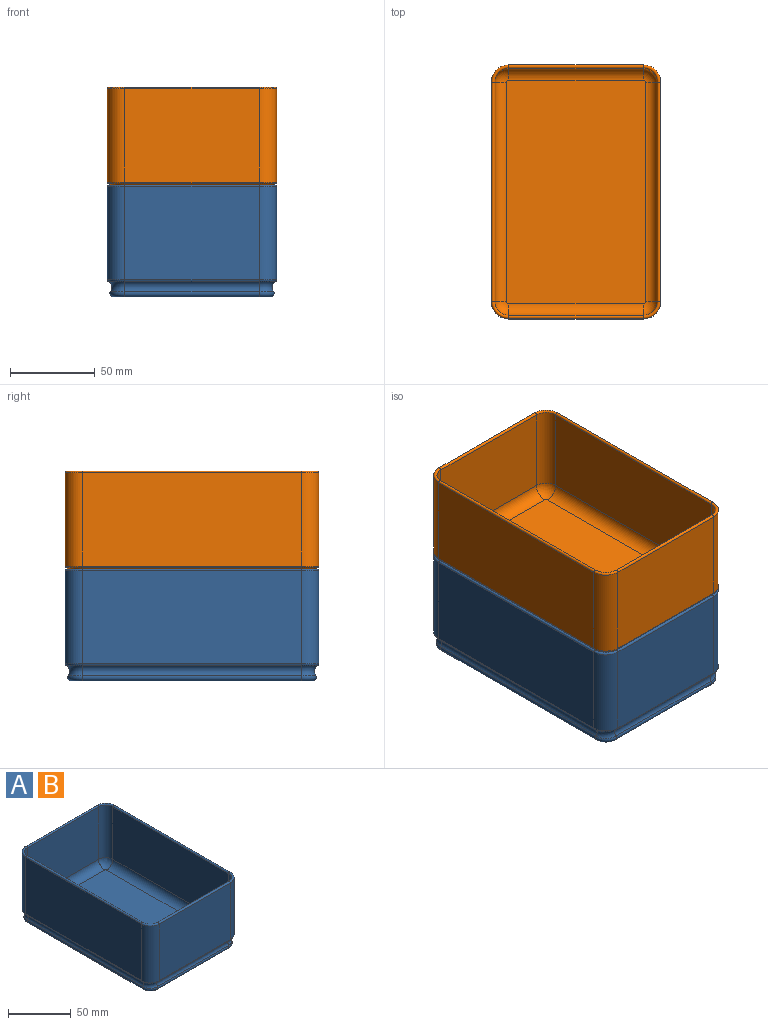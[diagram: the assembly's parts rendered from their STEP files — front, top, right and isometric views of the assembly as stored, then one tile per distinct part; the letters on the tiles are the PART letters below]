
ASSEMBLY  parts=2 mates=1
PART A: 66 faces, bbox 104.5x154.5x66 mm
  f0: torus R=0.68mm, axis (0,0,1), area 27mm2, adj f1,f8,f56,f65
  f1: torus R=6.6mm, axis (0,0,1), area 79.7mm2, adj f0,f2,f9,f57
  f2: torus R=11.42mm, axis (0,0,1), area 86.6mm2, adj f1,f3,f10,f58
  f3: torus R=9.1mm, axis (0,0,1), area 16.9mm2, adj f2,f4,f11,f59
  f4: cylinder r=10.1mm len=55mm, axis (0,0,1), area 872.6mm2, adj f3,f5,f12,f60
  f5: torus R=9.1mm, axis (0,0,1), area 44.9mm2, adj f4,f6,f13,f61
  f6: cylinder r=8.1mm len=51mm, axis (0,0,1), area 648.9mm2, adj f5,f7,f14,f62
  f7: torus R=1.1mm, axis (0,0,1), area 96mm2, adj f6,f15,f63,f64
  f8: cylinder r=4mm len=79.8mm, axis (-1,0,0), area 447.9mm2, adj f0,f9,f16,f65
  f9: cylinder r=2mm len=79.8mm, axis (-1,0,0), area 576.4mm2, adj f1,f8,f10,f17
  f10: cylinder r=4mm len=79.8mm, axis (-1,0,0), area 550.8mm2, adj f2,f9,f11,f18
  f11: cylinder r=1mm len=79.8mm, axis (-1,0,0), area 86.8mm2, adj f3,f10,f12,f19
  f12: plane 79.8x55mm, normal (0,1,0), area 4389mm2, adj f4,f11,f13,f20
  f13: cylinder r=1mm len=79.8mm, axis (-1,0,0), area 250.7mm2, adj f5,f12,f14,f21
  f14: plane 79.8x51mm, normal (0,-1,0), area 4069.8mm2, adj f6,f13,f15,f22
  f15: cylinder r=7mm len=79.8mm, axis (-1,0,0), area 877.4mm2, adj f7,f14,f23,f64
  f16: torus R=0.68mm, axis (0,0,1), area 27mm2, adj f8,f17,f24,f65
  f17: torus R=6.6mm, axis (0,0,1), area 79.7mm2, adj f9,f16,f18,f25
  f18: torus R=11.42mm, axis (0,0,1), area 86.6mm2, adj f10,f17,f19,f26
  f19: torus R=9.1mm, axis (0,0,1), area 16.9mm2, adj f11,f18,f20,f27
  f20: cylinder r=10.1mm len=55mm, axis (0,0,1), area 872.6mm2, adj f12,f19,f21,f28
  f21: torus R=9.1mm, axis (0,0,1), area 44.9mm2, adj f13,f20,f22,f29
  f22: cylinder r=8.1mm len=51mm, axis (0,0,1), area 648.9mm2, adj f14,f21,f23,f30
  f23: torus R=1.1mm, axis (0,0,1), area 96mm2, adj f15,f22,f31,f64
  f24: cylinder r=4mm len=129.8mm, axis (0,1,0), area 728.6mm2, adj f16,f25,f32,f65
  f25: cylinder r=2mm len=129.8mm, axis (0,1,0), area 937.6mm2, adj f17,f24,f26,f33
  f26: cylinder r=4mm len=129.8mm, axis (0,1,0), area 895.9mm2, adj f18,f25,f27,f34
  f27: cylinder r=1mm len=129.8mm, axis (0,1,0), area 141.2mm2, adj f19,f26,f28,f35
  f28: plane 129.8x55mm, normal (1,0,0), area 7139mm2, adj f20,f27,f29,f36
  f29: cylinder r=1mm len=129.8mm, axis (0,1,0), area 407.8mm2, adj f21,f28,f30,f37
  f30: plane 129.8x51mm, normal (-1,0,0), area 6619.8mm2, adj f22,f29,f31,f38
  f31: cylinder r=7mm len=129.8mm, axis (0,1,0), area 1427.2mm2, adj f23,f30,f39,f64
  f32: torus R=0.68mm, axis (0,0,1), area 27mm2, adj f24,f33,f40,f65
  f33: torus R=6.6mm, axis (0,0,1), area 79.7mm2, adj f25,f32,f34,f41
  f34: torus R=11.42mm, axis (0,0,1), area 86.6mm2, adj f26,f33,f35,f42
  f35: torus R=9.1mm, axis (0,0,1), area 16.9mm2, adj f27,f34,f36,f43
  f36: cylinder r=10.1mm len=55mm, axis (0,0,1), area 872.6mm2, adj f28,f35,f37,f44
  f37: torus R=9.1mm, axis (0,0,1), area 44.9mm2, adj f29,f36,f38,f45
  f38: cylinder r=8.1mm len=51mm, axis (0,0,1), area 648.9mm2, adj f30,f37,f39,f46
  f39: torus R=1.1mm, axis (0,0,1), area 96mm2, adj f31,f38,f47,f64
  f40: cylinder r=4mm len=79.8mm, axis (1,0,0), area 447.9mm2, adj f32,f41,f48,f65
  f41: cylinder r=2mm len=79.8mm, axis (1,0,0), area 576.4mm2, adj f33,f40,f42,f49
  f42: cylinder r=4mm len=79.8mm, axis (1,0,0), area 550.8mm2, adj f34,f41,f43,f50
  f43: cylinder r=1mm len=79.8mm, axis (1,0,0), area 86.8mm2, adj f35,f42,f44,f51
  f44: plane 79.8x55mm, normal (0,-1,0), area 4389mm2, adj f36,f43,f45,f52
  f45: cylinder r=1mm len=79.8mm, axis (1,0,0), area 250.7mm2, adj f37,f44,f46,f53
  f46: plane 79.8x51mm, normal (0,1,0), area 4069.8mm2, adj f38,f45,f47,f54
  f47: cylinder r=7mm len=79.8mm, axis (1,0,0), area 877.4mm2, adj f39,f46,f55,f64
  f48: torus R=0.68mm, axis (0,0,1), area 27mm2, adj f40,f49,f56,f65
  f49: torus R=6.6mm, axis (0,0,1), area 79.7mm2, adj f41,f48,f50,f57
  f50: torus R=11.42mm, axis (0,0,1), area 86.6mm2, adj f42,f49,f51,f58
  f51: torus R=9.1mm, axis (0,0,1), area 16.9mm2, adj f43,f50,f52,f59
  f52: cylinder r=10.1mm len=55mm, axis (0,0,1), area 872.6mm2, adj f44,f51,f53,f60
  f53: torus R=9.1mm, axis (0,0,1), area 44.9mm2, adj f45,f52,f54,f61
  f54: cylinder r=8.1mm len=51mm, axis (0,0,1), area 648.9mm2, adj f46,f53,f55,f62
  f55: torus R=1.1mm, axis (0,0,1), area 96mm2, adj f47,f54,f63,f64
  f56: cylinder r=4mm len=129.8mm, axis (0,-1,0), area 728.6mm2, adj f0,f48,f57,f65
  f57: cylinder r=2mm len=129.8mm, axis (0,-1,0), area 937.6mm2, adj f1,f49,f56,f58
  f58: cylinder r=4mm len=129.8mm, axis (0,-1,0), area 895.9mm2, adj f2,f50,f57,f59
  f59: cylinder r=1mm len=129.8mm, axis (0,-1,0), area 141.2mm2, adj f3,f51,f58,f60
  f60: plane 129.8x55mm, normal (-1,0,0), area 7139mm2, adj f4,f52,f59,f61
  f61: cylinder r=1mm len=129.8mm, axis (0,-1,0), area 407.8mm2, adj f5,f53,f60,f62
  f62: plane 129.8x51mm, normal (1,0,0), area 6619.8mm2, adj f6,f54,f61,f63
  f63: cylinder r=7mm len=129.8mm, axis (0,-1,0), area 1427.2mm2, adj f7,f55,f62,f64
  f64: plane 132x82mm, normal (0,0,1), area 10823mm2, adj f7,f15,f23,f31,f39,f47,f55,f63
  f65: plane 131.17x81.17mm, normal (0,0,-1), area 10646.2mm2, adj f0,f8,f16,f24,f32,f40,f48,f56
PART B: same geometry as A
PLACE A t=(-89.53,-11.77,31.88)mm fixed
PLACE B t=(-89.53,-11.77,89.69)mm
MATE slider B.f64 <-> A.f64  axis (0,0,1) through (-89.53,-11.77,91.69)mm
